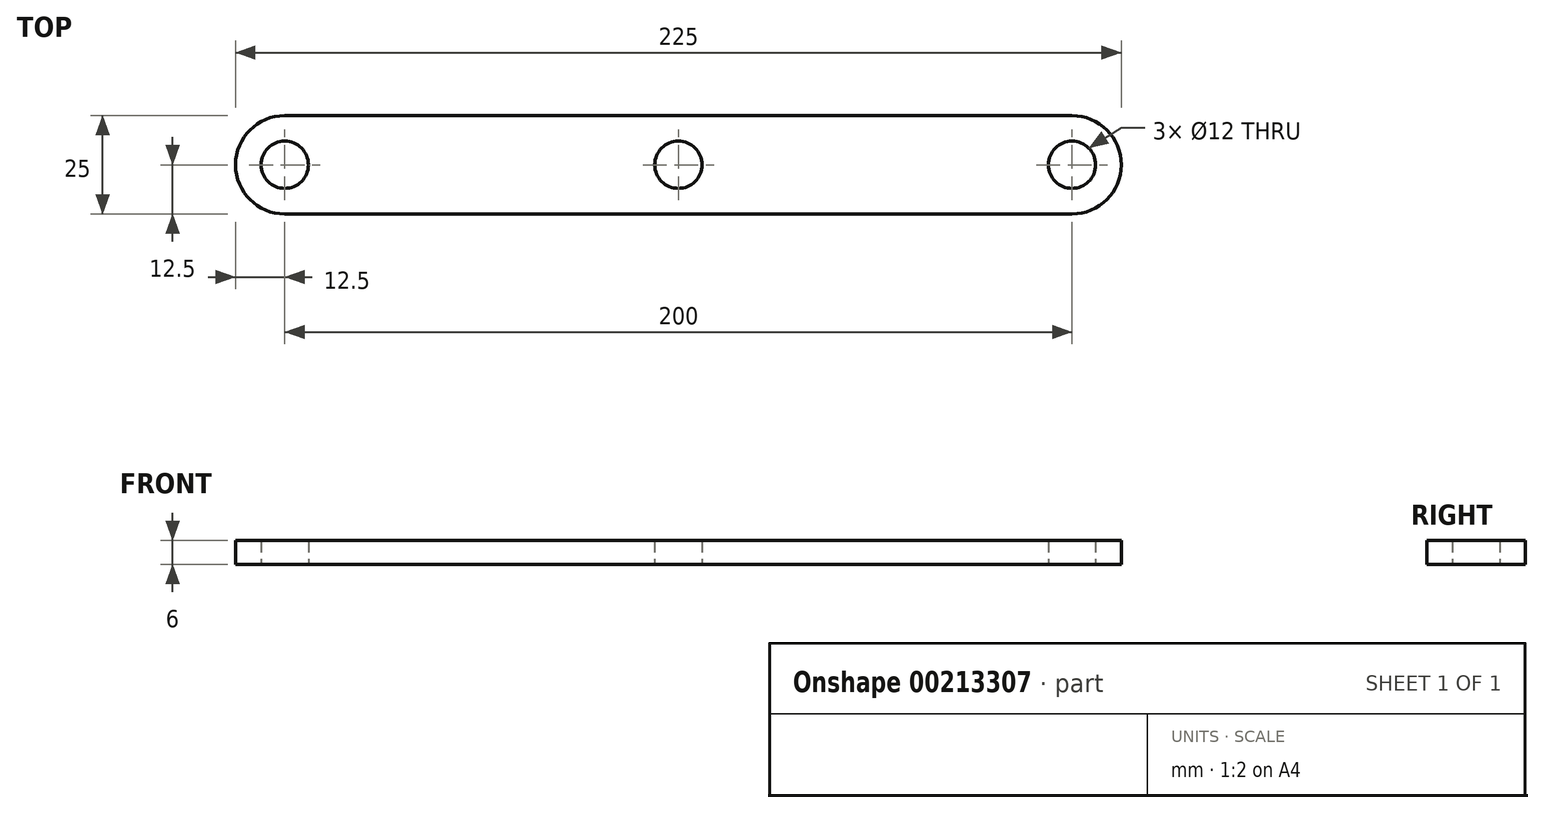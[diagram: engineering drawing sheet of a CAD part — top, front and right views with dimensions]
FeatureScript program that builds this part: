
annotation { "Feature Type Name" : "Feature", "Feature Type Description" : "" }
export const myFeature = defineFeature(function(context is Context, id is Id, definition is map)
    precondition{}
    {
        {
            var Q0;
            Q0=qCreatedBy(makeId("Top.planeOp"),FACE);
            var sketch = newSketch(context, id + "F0", { "sketchPlane" : qUnion([Q0])});
            skCircle(sketch, "E0", {"center": v(-100, 0) * mm, "radius": 6 * mm});
            skCircle(sketch, "E1", {"center": v(100, 0) * mm, "radius": 6 * mm});
            skArc(sketch, "E2", {"start": v(-100, 12.5) * mm, "mid": v(-112.5, 0) * mm, "end": v(-100, -12.5) * mm});
            skArc(sketch, "E3", {"start": v(100, -12.5) * mm, "mid": v(112.5, 0) * mm, "end": v(100, 12.5) * mm});
            skLineSegment(sketch, "E4", {"start": v(-100, -12.5) * mm, "end": v(100, -12.5) * mm});
            skLineSegment(sketch, "E5", {"start": v(100, 12.5) * mm, "end": v(-100, 12.5) * mm});
            skCircle(sketch, "E6", {"center": v(0, 0) * mm, "radius": 6 * mm});
            skSolve(sketch);
        }
        {
            var Q0;
            Q0=makeQuery(id+"F0.imprint","IMPRINT",FACE,{"disambiguationData":[TD([[makeQuery(id+"F0.imprint","IMPRINT",EDGE,{"derivedFrom":sQuery(id+"F0.wireOp",EDGE,"E0")}),-1.0]])]});
            extrude(context, id + "F1", {"entities" : qUnion([Q0]), "depth" : 6 * mm});
        }
    });
